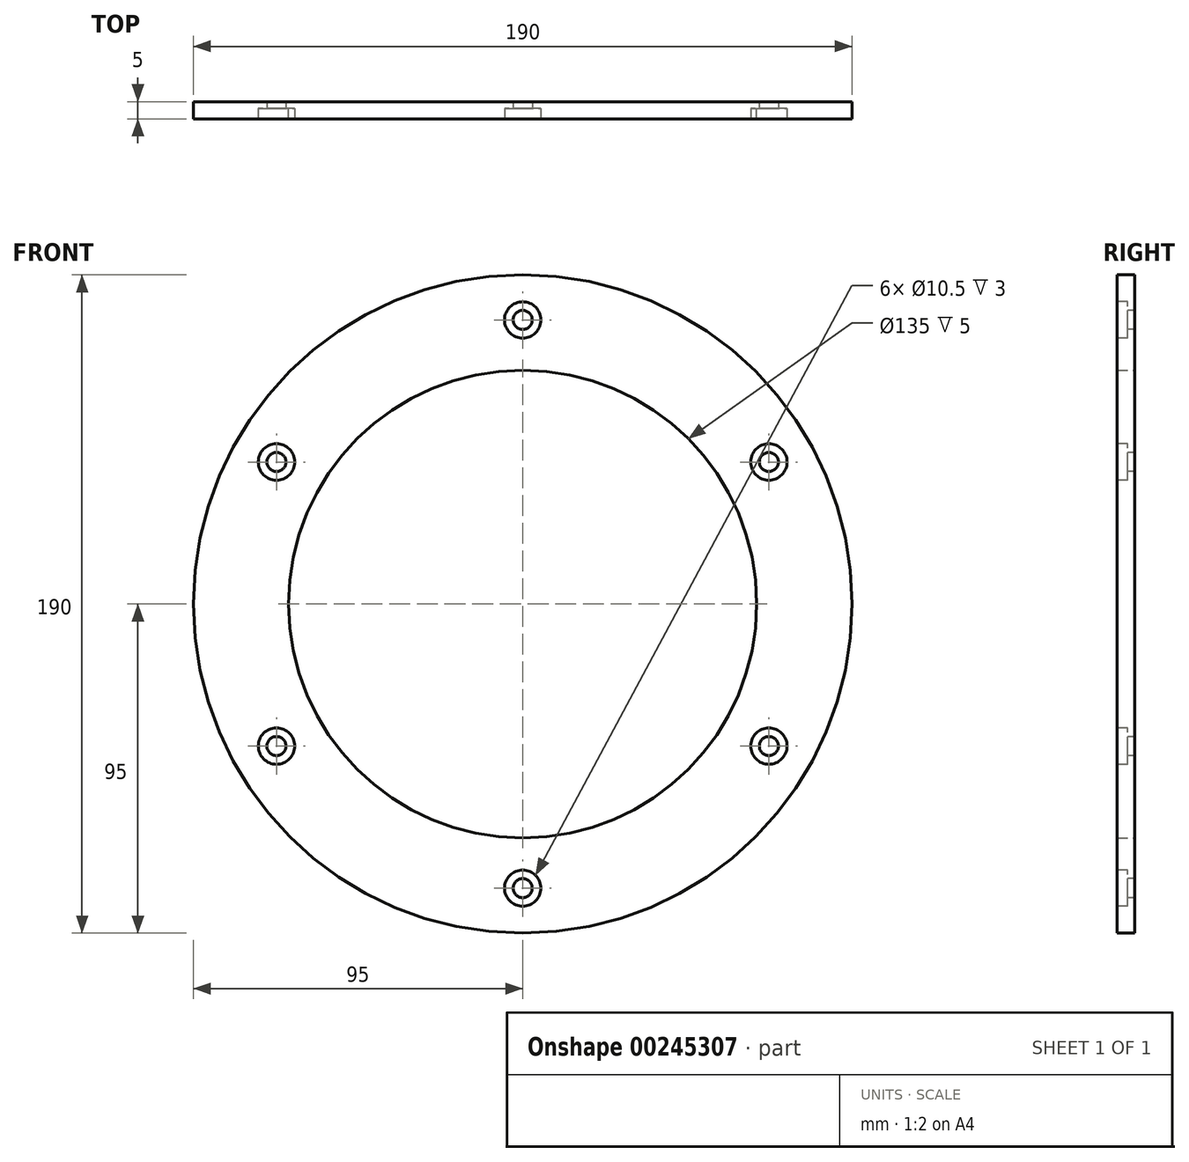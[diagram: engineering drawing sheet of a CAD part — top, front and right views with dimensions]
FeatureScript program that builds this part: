
annotation { "Feature Type Name" : "Feature", "Feature Type Description" : "" }
export const myFeature = defineFeature(function(context is Context, id is Id, definition is map)
    precondition{}
    {
        {
            var Q0;
            Q0=qCreatedBy(makeId("Front.planeOp"),FACE);
            var sketch = newSketch(context, id + "F0", { "sketchPlane" : qUnion([Q0])});
            skCircle(sketch, "E0", {"center": v(0, 0) * mm, "radius": 95 * mm});
            skCircle(sketch, "E1", {"center": v(0, 0) * mm, "radius": 67.5 * mm});
            skSolve(sketch);
        }
        {
            var Q0;
            Q0=makeQuery(id+"F0.imprint","IMPRINT",FACE,{"disambiguationData":[TD([[makeQuery(id+"F0.imprint","IMPRINT",EDGE,{"derivedFrom":sQuery(id+"F0.wireOp",EDGE,"E0")}),1.0]])]});
            extrude(context, id + "F1", {"entities" : qUnion([Q0]), "depth" : 5 * mm, "offsetDistance" : 25 * mm});
        }
        {
            var Q0;
            Q0=makeQuery(id+"F1.opExtrude","CAP_FACE",FACE,{"disambiguationData":[OSD([sQuery(id+"F0.wireOp",EDGE,"E0"),sQuery(id+"F0.wireOp",EDGE,"E1")])],"isStart":false});
            var sketch = newSketch(context, id + "F2", { "sketchPlane" : qUnion([Q0])});
            skPoint(sketch, "E2", {"position": v(0, 82) * mm});
            skPoint(sketch, "E3.1.0", {"position": v(-71.01, 41) * mm});
            skPoint(sketch, "E3.2.0", {"position": v(-71.01, -41) * mm});
            skPoint(sketch, "E3.3.0", {"position": v(0, -82) * mm});
            skPoint(sketch, "E3.4.0", {"position": v(71.01, -41) * mm});
            skPoint(sketch, "E3.5.0", {"position": v(71.01, 41) * mm});
            skPoint(sketch, "E3.center", {"position": v(0, 0) * mm});
            skSolve(sketch);
        }
        {
            var Q0;
            Q0=sQuery(id+"F2.wireOp",VERTEX,"E2");
            var Q1;
            Q1=sQuery(id+"F2.wireOp",VERTEX,"E3.1.0");
            var Q2;
            Q2=sQuery(id+"F2.wireOp",VERTEX,"E3.2.0");
            var Q3;
            Q3=sQuery(id+"F2.wireOp",VERTEX,"E3.4.0");
            var Q4;
            Q4=sQuery(id+"F2.wireOp",VERTEX,"E3.5.0");
            var Q5;
            Q5=sQuery(id+"F2.wireOp",VERTEX,"E3.3.0");
            var Q6;
            Q6=makeQuery(id+"F1.opExtrude","SWEPT_BODY",BODY,{"disambiguationData":[OSD([sQuery(id+"F0.wireOp",EDGE,"E0"),sQuery(id+"F0.wireOp",EDGE,"E1")])]});
            hole(context, id + "F3", {"style" : HoleStyle.C_BORE, "endStyle" : HoleEndStyle.THROUGH, "holeDiameter" : 5.5 * mm, "cBoreDiameter" : 10.5 * mm, "cBoreDepth" : 3 * mm, "majorDiameter" : 5 * mm, "isTappedThrough" : true, "tappedDepth" : 31.25 * mm, "tapClearance" : 3, "startFromSketch" : true, "locations" : qUnion([Q0, Q1, Q2, Q3, Q4, Q5]), "scope" : qUnion([Q6])});
        }
    });
